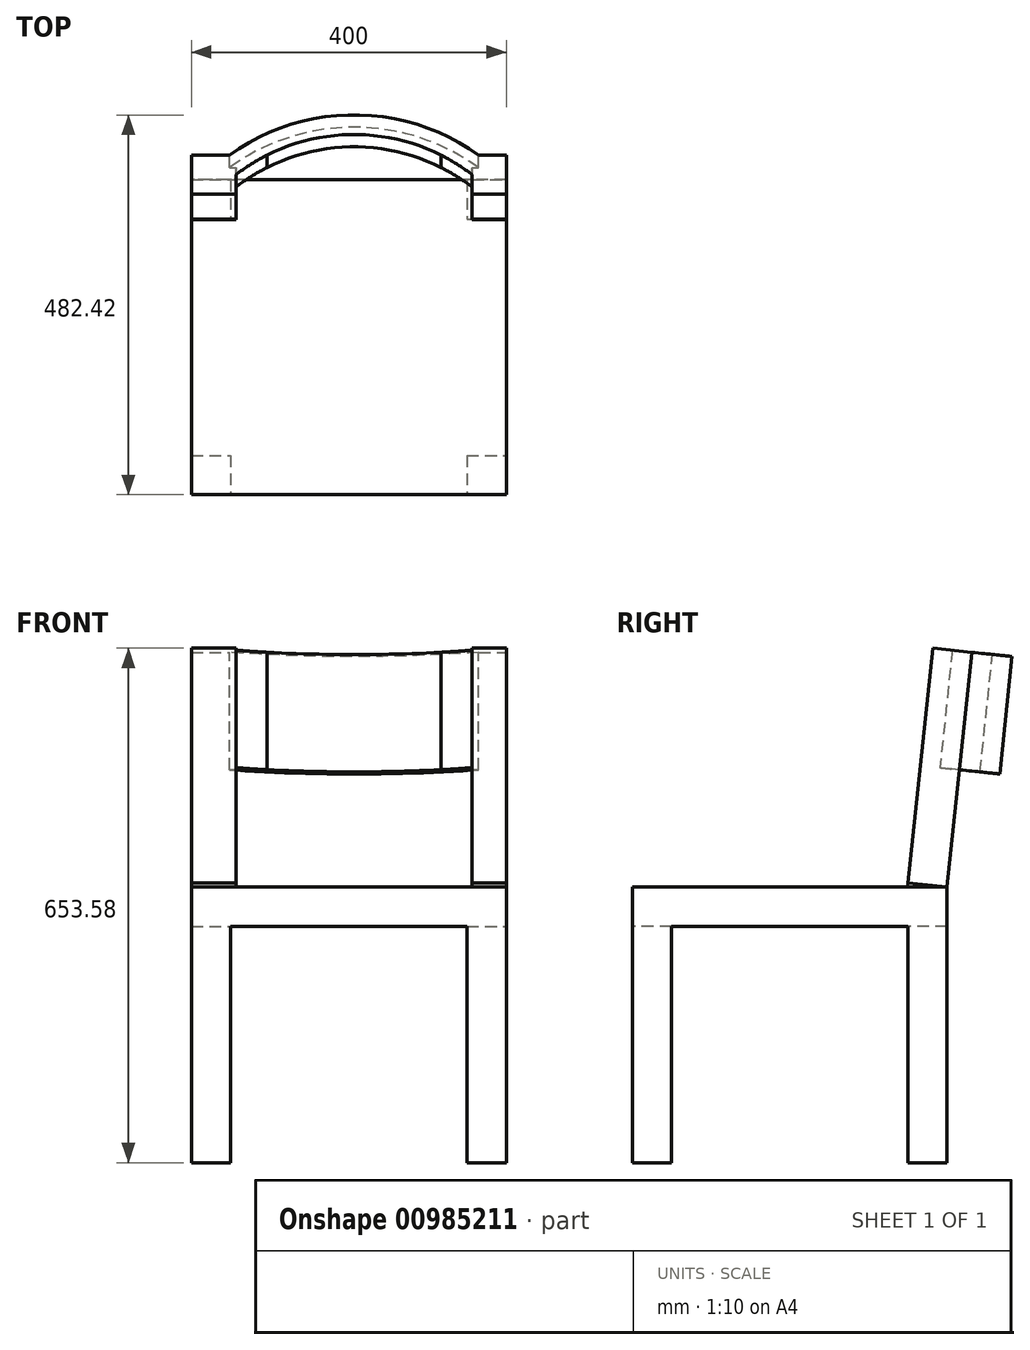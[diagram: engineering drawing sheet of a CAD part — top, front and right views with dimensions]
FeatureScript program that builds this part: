
annotation { "Feature Type Name" : "Feature", "Feature Type Description" : "" }
export const myFeature = defineFeature(function(context is Context, id is Id, definition is map)
    precondition{}
    {
        {
            var Q0;
            Q0=qCreatedBy(makeId("Top.planeOp"),FACE);
            var sketch = newSketch(context, id + "F0", { "sketchPlane" : qUnion([Q0])});
            skLineSegment(sketch, "E0.bottom", {"start": v(200, 200) * mm, "end": v(-200, 200) * mm});
            skLineSegment(sketch, "E0.top", {"start": v(200, -200) * mm, "end": v(-200, -200) * mm});
            skLineSegment(sketch, "E0.left", {"start": v(200, 200) * mm, "end": v(200, -200) * mm});
            skLineSegment(sketch, "E0.right", {"start": v(-200, 200) * mm, "end": v(-200, -200) * mm});
            skPoint(sketch, "E0.middle", {"position": v(0, 0) * mm});
            skSolve(sketch);
        }
        {
            var Q0;
            Q0=makeQuery(id+"F0.imprint","IMPRINT",FACE,{"disambiguationData":[TD([[makeQuery(id+"F0.imprint","IMPRINT",EDGE,{"derivedFrom":sQuery(id+"F0.wireOp",EDGE,"E0.bottom")}),1.0]])]});
            extrude(context, id + "F1", {"entities" : qUnion([Q0]), "depth" : 350 * mm, "offsetDistance" : 25 * mm});
        }
        {
            var Q0;
            Q0=makeQuery(id+"F1.opExtrude","SWEPT_FACE",FACE,{"disambiguationData":[OSD([sQuery(id+"F0.wireOp",EDGE,"E0.left")])]});
            var sketch = newSketch(context, id + "F2", { "sketchPlane" : qUnion([Q0])});
            skLineSegment(sketch, "E1.bottom", {"start": v(0, 0) * mm, "end": v(-150, 0) * mm});
            skLineSegment(sketch, "E1.top", {"start": v(0, 300) * mm, "end": v(-150, 300) * mm});
            skLineSegment(sketch, "E1.left", {"start": v(0, 0) * mm, "end": v(0, 300) * mm});
            skLineSegment(sketch, "E1.right", {"start": v(-150, 0) * mm, "end": v(-150, 300) * mm});
            skSolve(sketch);
        }
        {
            var Q0;
            Q0=makeQuery(id+"F2.imprint","IMPRINT",FACE,{"disambiguationData":[TD([[makeQuery(id+"F2.imprint","IMPRINT",EDGE,{"derivedFrom":sQuery(id+"F2.wireOp",EDGE,"E1.bottom")}),-1.0]])]});
            extrude(context, id + "F3", {"entities" : qUnion([Q0]), "operationType" : NewBodyOperationType.REMOVE, "oppositeDirection" : true, "depth" : 523 * mm, "offsetDistance" : 25 * mm});
        }
        {
            var Q0;
            Q0=makeQuery(id+"F1.opExtrude","SWEPT_FACE",FACE,{"disambiguationData":[OSD([sQuery(id+"F0.wireOp",EDGE,"E0.left")])]});
            var sketch = newSketch(context, id + "F4", { "sketchPlane" : qUnion([Q0])});
            skLineSegment(sketch, "E2.bottom", {"start": v(0, 0) * mm, "end": v(150, 0) * mm});
            skLineSegment(sketch, "E2.top", {"start": v(0, 300) * mm, "end": v(150, 300) * mm});
            skLineSegment(sketch, "E2.left", {"start": v(0, 0) * mm, "end": v(0, 300) * mm});
            skLineSegment(sketch, "E2.right", {"start": v(150, 0) * mm, "end": v(150, 300) * mm});
            skSolve(sketch);
        }
        {
            var Q0;
            Q0=makeQuery(id+"F4.imprint","IMPRINT",FACE,{"disambiguationData":[TD([[makeQuery(id+"F4.imprint","IMPRINT",EDGE,{"derivedFrom":sQuery(id+"F4.wireOp",EDGE,"E2.bottom")}),-1.0]])]});
            extrude(context, id + "F5", {"entities" : qUnion([Q0]), "operationType" : NewBodyOperationType.REMOVE, "oppositeDirection" : true, "depth" : 523 * mm, "offsetDistance" : 25 * mm});
        }
        {
            var Q0;
            Q0=makeQuery(id+"F1.opExtrude","SWEPT_FACE",FACE,{"disambiguationData":[OSD([sQuery(id+"F0.wireOp",EDGE,"E0.top")])]});
            var sketch = newSketch(context, id + "F6", { "sketchPlane" : qUnion([Q0])});
            skLineSegment(sketch, "E3.bottom", {"start": v(0, 0) * mm, "end": v(-150, 0) * mm});
            skLineSegment(sketch, "E3.top", {"start": v(0, 300) * mm, "end": v(-150, 300) * mm});
            skLineSegment(sketch, "E3.left", {"start": v(0, 0) * mm, "end": v(0, 300) * mm});
            skLineSegment(sketch, "E3.right", {"start": v(-150, 0) * mm, "end": v(-150, 300) * mm});
            skSolve(sketch);
        }
        {
            var Q0;
            {var subQ0=sQuery(id+"F6.wireOp",EDGE,"E3.top");Q0=makeQuery(id+"F6.imprint","IMPRINT",FACE,{"disambiguationData":[TD([[makeQuery(id+"F6.imprint","IMPRINT",EDGE,{"derivedFrom":subQ0}),1.0]])]});}
            extrude(context, id + "F7", {"entities" : qUnion([Q0]), "operationType" : NewBodyOperationType.REMOVE, "oppositeDirection" : true, "depth" : 603 * mm, "offsetDistance" : 25 * mm});
        }
        {
            var Q0;
            Q0=makeQuery(id+"F1.opExtrude","CAP_FACE",FACE,{"disambiguationData":[OSD([sQuery(id+"F0.wireOp",EDGE,"E0.bottom"),sQuery(id+"F0.wireOp",EDGE,"E0.top"),sQuery(id+"F0.wireOp",EDGE,"E0.left"),sQuery(id+"F0.wireOp",EDGE,"E0.right")])],"isStart":false});
            var sketch = newSketch(context, id + "F8", { "sketchPlane" : qUnion([Q0])});
            skLineSegment(sketch, "E4.bottom", {"start": v(-200, 200) * mm, "end": v(-150, 200) * mm});
            skLineSegment(sketch, "E4.top", {"start": v(-200, -200) * mm, "end": v(-150, -200) * mm});
            skLineSegment(sketch, "E4.left", {"start": v(-200, 200) * mm, "end": v(-200, -200) * mm});
            skLineSegment(sketch, "E4.right", {"start": v(-150, 200) * mm, "end": v(-150, -200) * mm});
            skSolve(sketch);
        }
        {
            var Q0;
            Q0=makeQuery(id+"F8.imprint","IMPRINT",FACE,{"disambiguationData":[TD([[makeQuery(id+"F8.imprint","IMPRINT",EDGE,{"derivedFrom":sQuery(id+"F8.wireOp",EDGE,"E4.bottom")}),1.0]])]});
            extrude(context, id + "F9", {"entities" : qUnion([Q0]), "operationType" : NewBodyOperationType.ADD, "depth" : 300 * mm, "offsetDistance" : 25 * mm});
        }
        {
            var Q0;
            Q0=makeQuery(id+"F9.opExtrude","SWEPT_FACE",FACE,{"disambiguationData":[OSD([sQuery(id+"F8.wireOp",EDGE,"E4.right")])]});
            extrude(context, id + "F10", {"entities" : qUnion([Q0]), "operationType" : NewBodyOperationType.REMOVE, "oppositeDirection" : true, "depth" : 260 * mm, "offsetDistance" : 25 * mm});
        }
        {
            var Q0;
            {var subQ0=sQuery(id+"F8.wireOp",EDGE,"E4.right");Q0=makeQuery(id+"F10.boolean.opBoolean","MERGE",FACE,{"derivedFrom":[makeQuery(id+"F1.opExtrude","CAP_FACE",FACE,{"disambiguationData":[OSD([sQuery(id+"F0.wireOp",EDGE,"E0.bottom"),sQuery(id+"F0.wireOp",EDGE,"E0.top"),sQuery(id+"F0.wireOp",EDGE,"E0.left"),sQuery(id+"F0.wireOp",EDGE,"E0.right")])],"isStart":false})],"fromTools":[makeQuery(id+"F10.opExtrude","SWEPT_FACE",FACE,{"disambiguationData":[OSD([subQ0]),TDD([makeQuery(id+"F9.opExtrude","CAP_EDGE",EDGE,{"disambiguationData":[OSD([subQ0])],"isStart":true})])]})]});}
            cPlane(context, id + "F11", {"entities" : qUnion([Q0]), "cplaneType" : CPlaneType.OFFSET, "offset" : 0 * mm, "width" : 150 * mm, "height" : 150 * mm});
        }
        {
            var Q0;
            {var subQ0=sQuery(id+"F8.wireOp",EDGE,"E4.right");Q0=makeQuery(id+"F10.boolean.opBoolean","MERGE",FACE,{"derivedFrom":[makeQuery(id+"F1.opExtrude","CAP_FACE",FACE,{"disambiguationData":[OSD([sQuery(id+"F0.wireOp",EDGE,"E0.bottom"),sQuery(id+"F0.wireOp",EDGE,"E0.top"),sQuery(id+"F0.wireOp",EDGE,"E0.left"),sQuery(id+"F0.wireOp",EDGE,"E0.right")])],"isStart":false})],"fromTools":[makeQuery(id+"F10.opExtrude","SWEPT_FACE",FACE,{"disambiguationData":[OSD([subQ0]),TDD([makeQuery(id+"F9.opExtrude","CAP_EDGE",EDGE,{"disambiguationData":[OSD([subQ0])],"isStart":true})])]})]});}
            var sketch = newSketch(context, id + "F12", { "sketchPlane" : qUnion([Q0])});
            skSolve(sketch);
        }
        {
            var Q0;
            Q0=qCreatedBy(id+"F11.planeOp",FACE);
            var sketch = newSketch(context, id + "F13", { "sketchPlane" : qUnion([Q0])});
            skLineSegment(sketch, "E5", {"start": v(-214.18, 200) * mm, "end": v(227.3, 200) * mm});
            skSolve(sketch);
        }
        {
            var Q0;
            Q0=sQuery(id+"F13.wireOp",EDGE,"E5");
            cPlane(context, id + "F14", {"entities" : qUnion([Q0]), "cplaneType" : CPlaneType.LINE_ANGLE, "offset" : 25 * mm, "angle" : 6 * degree, "oppositeDirection" : true, "width" : 150 * mm, "height" : 150 * mm});
        }
        {
            var Q0;
            Q0=qCreatedBy(id+"F14.planeOp",FACE);
            var sketch = newSketch(context, id + "F15", { "sketchPlane" : qUnion([Q0])});
            skLineSegment(sketch, "E6.bottom", {"start": v(200, 368.99) * mm, "end": v(-200, 368.99) * mm});
            skLineSegment(sketch, "E6.top", {"start": v(200, 668.99) * mm, "end": v(-200, 668.99) * mm});
            skLineSegment(sketch, "E6.left", {"start": v(200, 368.99) * mm, "end": v(200, 668.99) * mm});
            skLineSegment(sketch, "E6.right", {"start": v(-200, 368.99) * mm, "end": v(-200, 668.99) * mm});
            skSolve(sketch);
        }
        {
            var Q0;
            Q0=makeQuery(id+"F15.imprint","IMPRINT",FACE,{"disambiguationData":[TD([[makeQuery(id+"F15.imprint","IMPRINT",EDGE,{"derivedFrom":sQuery(id+"F15.wireOp",EDGE,"E6.bottom")}),-1.0]])]});
            extrude(context, id + "F16", {"entities" : qUnion([Q0]), "oppositeDirection" : true, "depth" : 50 * mm, "offsetDistance" : 25 * mm});
        }
        {
            var Q0;
            Q0=makeQuery(id+"F16.opExtrude","CAP_FACE",FACE,{"disambiguationData":[OSD([sQuery(id+"F15.wireOp",EDGE,"E6.bottom"),sQuery(id+"F15.wireOp",EDGE,"E6.top"),sQuery(id+"F15.wireOp",EDGE,"E6.left"),sQuery(id+"F15.wireOp",EDGE,"E6.right")])],"isStart":false});
            var sketch = newSketch(context, id + "F17", { "sketchPlane" : qUnion([Q0])});
            skLineSegment(sketch, "E7.bottom", {"start": v(-143.44, 668.99) * mm, "end": v(156.56, 668.99) * mm});
            skLineSegment(sketch, "E7.top", {"start": v(-143.44, 368.99) * mm, "end": v(156.56, 368.99) * mm});
            skLineSegment(sketch, "E7.left", {"start": v(-143.44, 668.99) * mm, "end": v(-143.44, 368.99) * mm});
            skLineSegment(sketch, "E7.right", {"start": v(156.56, 668.99) * mm, "end": v(156.56, 368.99) * mm});
            skSolve(sketch);
        }
        {
            var Q0;
            Q0=makeQuery(id+"F17.imprint","IMPRINT",FACE,{"disambiguationData":[TD([[makeQuery(id+"F17.imprint","IMPRINT",EDGE,{"derivedFrom":sQuery(id+"F17.wireOp",EDGE,"E7.bottom")}),-1.0]])]});
            extrude(context, id + "F18", {"entities" : qUnion([Q0]), "operationType" : NewBodyOperationType.REMOVE, "depth" : 138 * mm, "offsetDistance" : 25 * mm});
        }
        {
            var Q0;
            Q0=makeQuery(id+"F6.imprint","IMPRINT",FACE,{"disambiguationData":[TD([[makeQuery(id+"F6.imprint","IMPRINT",EDGE,{"derivedFrom":sQuery(id+"F6.wireOp",EDGE,"E3.top")}),-1.0]])]});
            var sketch = newSketch(context, id + "F19", { "sketchPlane" : qUnion([Q0])});
            skLineSegment(sketch, "E8.bottom", {"start": v(0, 300) * mm, "end": v(150, 300) * mm});
            skLineSegment(sketch, "E8.top", {"start": v(0, 0) * mm, "end": v(150, 0) * mm});
            skLineSegment(sketch, "E8.left", {"start": v(0, 300) * mm, "end": v(0, 0) * mm});
            skLineSegment(sketch, "E8.right", {"start": v(150, 300) * mm, "end": v(150, 0) * mm});
            skSolve(sketch);
        }
        {
            var Q0;
            Q0=makeQuery(id+"F19.imprint","IMPRINT",FACE,{"disambiguationData":[TD([[makeQuery(id+"F19.imprint","IMPRINT",EDGE,{"derivedFrom":sQuery(id+"F19.wireOp",EDGE,"E8.bottom")}),-1.0]])]});
            extrude(context, id + "F20", {"entities" : qUnion([Q0]), "operationType" : NewBodyOperationType.REMOVE, "endBound" : BoundingType.THROUGH_ALL, "oppositeDirection" : true, "depth" : 25 * mm, "offsetDistance" : 25 * mm});
        }
        {
            var Q0;
            Q0=makeQuery(id+"F17.imprint","IMPRINT",FACE,{"disambiguationData":[TD([[makeQuery(id+"F17.imprint","IMPRINT",EDGE,{"derivedFrom":sQuery(id+"F17.wireOp",EDGE,"E7.bottom")}),-1.0]])]});
            var sketch = newSketch(context, id + "F21", { "sketchPlane" : qUnion([Q0])});
            skLineSegment(sketch, "E9.bottom", {"start": v(-143.44, 368.99) * mm, "end": v(156.56, 368.99) * mm});
            skLineSegment(sketch, "E9.top", {"start": v(-143.44, 518.99) * mm, "end": v(156.56, 518.99) * mm});
            skLineSegment(sketch, "E9.left", {"start": v(-143.44, 368.99) * mm, "end": v(-143.44, 518.99) * mm});
            skLineSegment(sketch, "E9.right", {"start": v(156.56, 368.99) * mm, "end": v(156.56, 518.99) * mm});
            skSolve(sketch);
        }
        {
            var Q0;
            Q0=makeQuery(id+"F21.imprint","IMPRINT",FACE,{"disambiguationData":[TD([[makeQuery(id+"F21.imprint","IMPRINT",EDGE,{"derivedFrom":sQuery(id+"F21.wireOp",EDGE,"E9.bottom")}),1.0]])]});
            extrude(context, id + "F22", {"entities" : qUnion([Q0]), "operationType" : NewBodyOperationType.REMOVE, "endBound" : BoundingType.THROUGH_ALL, "oppositeDirection" : true, "depth" : 25 * mm, "offsetDistance" : 25 * mm});
        }
        {
            var Q0;
            {var subQ1=sQuery(id+"F15.wireOp",EDGE,"E6.left");var subQ3=sQuery(id+"F15.wireOp",EDGE,"E6.bottom");Q0=makeQuery(id+"F22.boolean.opBoolean","SPLIT",FACE,{"disambiguationData":[TD([makeQuery(id+"F16.opExtrude","SWEPT_FACE",FACE,{"disambiguationData":[OSD([subQ1])]})])],"derivedFrom":makeQuery(id+"F16.opExtrude","SWEPT_FACE",FACE,{"disambiguationData":[OSD([subQ3])]})});}
            var Q1;
            {var subQ0=sQuery(id+"F15.wireOp",EDGE,"E6.right");var subQ3=sQuery(id+"F15.wireOp",EDGE,"E6.bottom");Q1=makeQuery(id+"F22.boolean.opBoolean","SPLIT",FACE,{"disambiguationData":[TD([makeQuery(id+"F16.opExtrude","SWEPT_FACE",FACE,{"disambiguationData":[OSD([subQ0])]})])],"derivedFrom":makeQuery(id+"F16.opExtrude","SWEPT_FACE",FACE,{"disambiguationData":[OSD([subQ3])]})});}
            extrude(context, id + "F23", {"entities" : qUnion([Q0, Q1]), "endBound" : BoundingType.UP_TO_NEXT, "depth" : 25 * mm, "offsetDistance" : 25 * mm});
        }
        {
            var Q0;
            Q0=makeQuery(id+"F17.imprint","IMPRINT",FACE,{"disambiguationData":[TD([[makeQuery(id+"F17.imprint","IMPRINT",EDGE,{"derivedFrom":sQuery(id+"F17.wireOp",EDGE,"E7.bottom")}),-1.0]])]});
            extrude(context, id + "F24", {"entities" : qUnion([Q0]), "operationType" : NewBodyOperationType.REMOVE, "oppositeDirection" : true, "depth" : 25 * mm, "offsetDistance" : 25 * mm});
        }
        {
            var Q0;
            Q0=makeQuery(id+"F16.opExtrude","SWEPT_FACE",FACE,{"disambiguationData":[OSD([sQuery(id+"F15.wireOp",EDGE,"E6.top")])]});
            var sketch = newSketch(context, id + "F25", { "sketchPlane" : qUnion([Q0])});
            skArc(sketch, "E10", {"start": v(156.56, 137.32) * mm, "mid": v(6.56, 188.66) * mm, "end": v(-143.44, 137.32) * mm});
            skArc(sketch, "E11.0", {"start": v(171.88, 157.08) * mm, "mid": v(6.56, 213.66) * mm, "end": v(-158.76, 157.08) * mm});
            skLineSegment(sketch, "E12", {"start": v(-158.76, 157.08) * mm, "end": v(-143.44, 137.32) * mm});
            skLineSegment(sketch, "E13", {"start": v(171.88, 157.08) * mm, "end": v(156.56, 137.32) * mm});
            skSolve(sketch);
        }
        {
            var Q0;
            {var subQ0=sQuery(id+"F25.wireOp",EDGE,"E10");var subQ1=makeQuery(id+"F16.opExtrude","CAP_EDGE",EDGE,{"disambiguationData":[OSD([sQuery(id+"F15.wireOp",EDGE,"E6.top")])],"isStart":true});var subQ2=makeQuery(id+"F25.imprint","INTERSECT",VERTEX,{"disambiguationData":[OD(0.0)],"derivedFrom":[subQ1,subQ0]});Q0=makeQuery(id+"F25.imprint","IMPRINT",FACE,{"disambiguationData":[TD([[makeQuery(id+"F25.imprint","IMPRINT",EDGE,{"disambiguationData":[TD([[subQ2,-1.0]])],"derivedFrom":subQ0}),-1.0]])]});}
            extrude(context, id + "F26", {"entities" : qUnion([Q0]), "operationType" : NewBodyOperationType.ADD, "oppositeDirection" : true, "depth" : 150 * mm, "offsetDistance" : 25 * mm});
        }
        {
            var Q0;
            {var subQ0=sQuery(id+"F15.wireOp",EDGE,"E6.top");Q0=makeQuery(id+"F26.boolean.opBoolean","MERGE",FACE,{"derivedFrom":[makeQuery(id+"F16.opExtrude","SWEPT_FACE",FACE,{"disambiguationData":[OSD([subQ0])]}),makeQuery(id+"F26.opExtrude","CAP_FACE",FACE,{"disambiguationData":[OSD([subQ0,sQuery(id+"F25.wireOp",EDGE,"E10"),sQuery(id+"F25.wireOp",EDGE,"E11.0")])],"isStart":true})]});}
            var sketch = newSketch(context, id + "F27", { "sketchPlane" : qUnion([Q0])});
            skArc(sketch, "E14", {"start": v(156.56, 137.32) * mm, "mid": v(6.56, 188.62) * mm, "end": v(-143.44, 137.32) * mm});
            skLineSegment(sketch, "E15", {"start": v(-143.44, 137.32) * mm, "end": v(156.56, 137.32) * mm});
            skSolve(sketch);
        }
        {
            var Q0;
            {var subQ0=sQuery(id+"F27.wireOp",EDGE,"E15");Q0=makeQuery(id+"F27.imprint","IMPRINT",FACE,{"disambiguationData":[TD([[makeQuery(id+"F27.imprint","IMPRINT",EDGE,{"derivedFrom":subQ0}),1.0]])]});}
            extrude(context, id + "F28", {"entities" : qUnion([Q0]), "operationType" : NewBodyOperationType.REMOVE, "oppositeDirection" : true, "depth" : 150 * mm, "offsetDistance" : 25 * mm});
        }
    });
